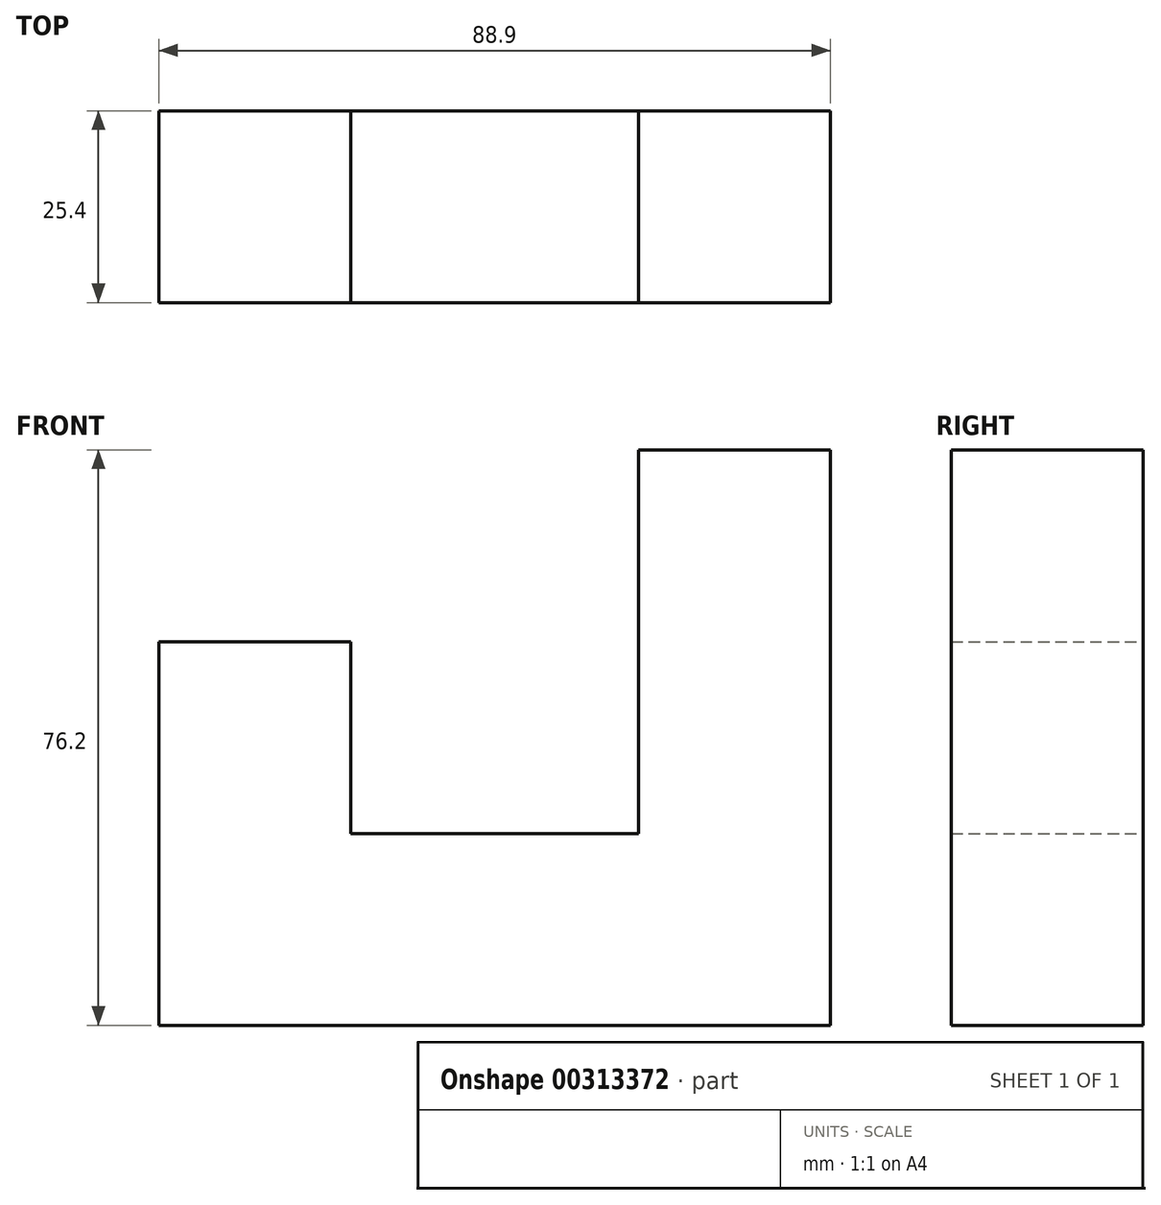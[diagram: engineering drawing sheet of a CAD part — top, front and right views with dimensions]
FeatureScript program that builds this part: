
annotation { "Feature Type Name" : "Feature", "Feature Type Description" : "" }
export const myFeature = defineFeature(function(context is Context, id is Id, definition is map)
    precondition{}
    {
        {
            var Q0;
            Q0=qCreatedBy(makeId("Front.planeOp"),FACE);
            var sketch = newSketch(context, id + "F0", { "sketchPlane" : qUnion([Q0])});
            skLineSegment(sketch, "E0", {"start": v(-33.14, -31.6) * mm, "end": v(55.76, -31.6) * mm});
            skLineSegment(sketch, "E1", {"start": v(-33.14, -31.6) * mm, "end": v(-33.14, 19.2) * mm});
            skLineSegment(sketch, "E2", {"start": v(-33.14, 19.2) * mm, "end": v(-7.74, 19.2) * mm});
            skLineSegment(sketch, "E3", {"start": v(-7.74, 19.2) * mm, "end": v(-7.74, -6.2) * mm});
            skLineSegment(sketch, "E4", {"start": v(-7.74, -6.2) * mm, "end": v(30.36, -6.2) * mm});
            skLineSegment(sketch, "E5", {"start": v(30.36, -6.2) * mm, "end": v(30.36, 44.6) * mm});
            skLineSegment(sketch, "E6", {"start": v(30.36, 44.6) * mm, "end": v(55.76, 44.6) * mm});
            skLineSegment(sketch, "E7", {"start": v(55.76, 44.6) * mm, "end": v(55.76, -31.6) * mm});
            skSolve(sketch);
        }
        {
            var Q0;
            Q0=makeQuery(id+"F0.imprint","IMPRINT",FACE,{"disambiguationData":[TD([[makeQuery(id+"F0.imprint","IMPRINT",EDGE,{"derivedFrom":sQuery(id+"F0.wireOp",EDGE,"E0")}),1.0]])]});
            extrude(context, id + "F1", {"entities" : qUnion([Q0]), "depth" : 25.4 * mm});
        }
    });
